# Revit family: QF_ADVENTYS_ADV1712-A_KNL4S_8000_Front_to_Back
name_source: partatom
category: Attrezzature speciali
units: mm (PartAtom-declared; Revit-internal decimal feet)

## family parameters
Condiviso = No
Host = Superficie
Punto di calcolo locali = No
Quota connettore circolare = Usa diametro
Taglio con vuoti quando caricato = No
Tipo di parte = Normale

## types (1)
- ADV1712-A
    Controller_Height = 120 mm  [stored 0.393701 ft]
    Controller_Width = 250 mm  [stored 0.82021 ft]
    Cycle = 50 Hz
    Depth = 690 mm  [stored 2.26378 ft]
    Depth Actual = 220 mm  [stored 0.721785 ft]
    Height = 79.3 mm  [stored 0.260171 ft]
    Height Actual = 79 mm
    Item Number = ADV1712-A
    Length Actual = 690 mm  [stored 2.26378 ft]
    Modello = KNL4S 8000 Front to Back
    Phase = 3
    Produttore = ADVENTYS
    Prospetto di default = 1219.2 mm  [stored 4 ft]
    URL = https://adventys.com
    Volts = 380 V
    Watts = 8000 W
    Weight = 15
    Width = 220 mm  [stored 0.721785 ft]

note: [stored X ft] marks values corroborated as IEEE doubles in the binary element streams (Revit-internal decimal feet)

## geometry (parser evidence)
native form markers: Blend x4, Sweep x2
no freeform markers — native parametric forms only
